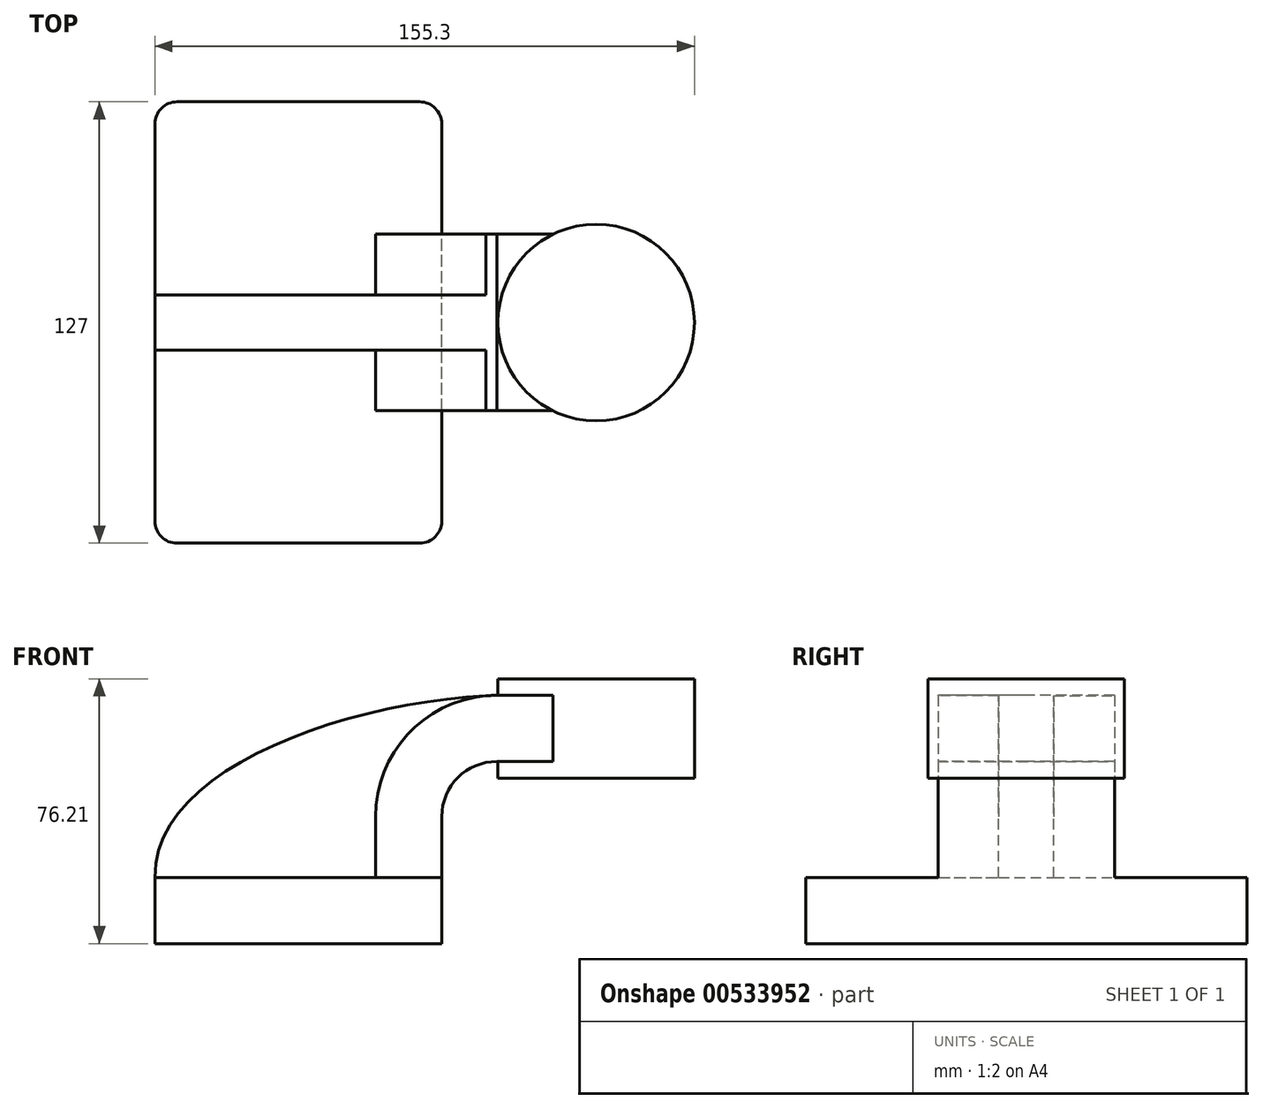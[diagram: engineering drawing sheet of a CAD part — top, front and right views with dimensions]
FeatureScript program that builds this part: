
annotation { "Feature Type Name" : "Feature", "Feature Type Description" : "" }
export const myFeature = defineFeature(function(context is Context, id is Id, definition is map)
    precondition{}
    {
        {
            var Q0;
            Q0=qCreatedBy(makeId("Front.planeOp"),FACE);
            var sketch = newSketch(context, id + "F0", { "sketchPlane" : qUnion([Q0])});
            skLineSegment(sketch, "E0.bottom", {"start": v(-41.28, 9.52) * mm, "end": v(41.27, 9.53) * mm});
            skLineSegment(sketch, "E0.top", {"start": v(-41.28, -9.52) * mm, "end": v(41.28, -9.52) * mm});
            skLineSegment(sketch, "E0.left", {"start": v(-41.28, 9.52) * mm, "end": v(-41.28, -9.53) * mm});
            skLineSegment(sketch, "E0.right", {"start": v(41.27, 9.53) * mm, "end": v(41.28, -9.52) * mm});
            skPoint(sketch, "E0.middle", {"position": v(0, 0) * mm});
            skLineSegment(sketch, "E1.bottom", {"start": v(63.22, 66.68) * mm, "end": v(114.02, 66.68) * mm});
            skLineSegment(sketch, "E1.top", {"start": v(63.22, 38.1) * mm, "end": v(114.02, 38.1) * mm});
            skLineSegment(sketch, "E1.left", {"start": v(63.22, 66.68) * mm, "end": v(63.22, 38.1) * mm});
            skLineSegment(sketch, "E1.right", {"start": v(114.02, 66.68) * mm, "end": v(114.02, 38.1) * mm});
            skPoint(sketch, "E1.middle", {"position": v(88.62, 52.39) * mm});
            skLineSegment(sketch, "E2", {"start": v(41.27, 9.53) * mm, "end": v(41.27, 27) * mm});
            skArc(sketch, "E3", {"start": v(41.27, 27) * mm, "mid": v(45.92, 38.23) * mm, "end": v(57.15, 42.88) * mm});
            skLineSegment(sketch, "E4", {"start": v(57.15, 42.88) * mm, "end": v(85.72, 42.88) * mm});
            skLineSegment(sketch, "E5.0", {"start": v(57.15, 61.93) * mm, "end": v(85.72, 61.93) * mm});
            skArc(sketch, "E5.1", {"start": v(22.22, 27) * mm, "mid": v(32.45, 51.7) * mm, "end": v(57.15, 61.93) * mm});
            skLineSegment(sketch, "E5.2", {"start": v(22.22, 9.53) * mm, "end": v(22.22, 27) * mm});
            skLineSegment(sketch, "E6", {"start": v(85.72, 38.1) * mm, "end": v(85.72, 61.93) * mm});
            skPoint(sketch, "E6.startSnap0", {"position": v(88.62, 38.1) * mm});
            skLineSegment(sketch, "E7", {"start": v(85.72, 61.93) * mm, "end": v(85.72, 66.68) * mm});
            skPoint(sketch, "E7.endSnap0", {"position": v(88.62, 66.68) * mm});
            skFitSpline(sketch, "E8", {"points": [v(-41.28, 9.52) * mm, v(57.15, 61.93) * mm], "startDerivative": vector(-1.63, 94.81) * mm, "endDerivative": vector(127.33, 4.49) * mm});
            skSolve(sketch);
        }
        {
            var Q0;
            Q0=makeQuery(id+"F0.imprint","IMPRINT",FACE,{"disambiguationData":[TD([[makeQuery(id+"F0.imprint","IMPRINT",EDGE,{"derivedFrom":sQuery(id+"F0.wireOp",EDGE,"E0.top")}),1.0]])]});
            extrude(context, id + "F1", {"entities" : qUnion([Q0]), "endBound" : BoundingType.SYMMETRIC, "depth" : 127 * mm, "offsetDistance" : 25.4 * mm});
        }
        {
            var Q0;
            {var subQ1=sQuery(id+"F0.wireOp",EDGE,"E2");Q0=makeQuery(id+"F0.imprint","IMPRINT",FACE,{"disambiguationData":[TD([[makeQuery(id+"F0.imprint","IMPRINT",EDGE,{"derivedFrom":subQ1}),1.0]])]});}
            var Q1;
            {var subQ0=sQuery(id+"F0.wireOp",EDGE,"E5.0");var subQ1=sQuery(id+"F0.wireOp",EDGE,"E1.left");var subQ2=makeQuery(id+"F0.imprint","INTERSECT",VERTEX,{"derivedFrom":[subQ1,subQ0]});Q1=makeQuery(id+"F0.imprint","IMPRINT",FACE,{"disambiguationData":[TD([[makeQuery(id+"F0.imprint","IMPRINT",EDGE,{"disambiguationData":[TD([[subQ2,-1.0]])],"derivedFrom":subQ1}),1.0]])]});}
            extrude(context, id + "F2", {"entities" : qUnion([Q0, Q1]), "operationType" : NewBodyOperationType.ADD, "endBound" : BoundingType.SYMMETRIC, "depth" : 50.8 * mm, "offsetDistance" : 25.4 * mm});
        }
        {
            var Q0;
            {var subQ3=sQuery(id+"F0.wireOp",EDGE,"E5.2");Q0=makeQuery(id+"F0.imprint","IMPRINT",FACE,{"disambiguationData":[TD([[makeQuery(id+"F0.imprint","IMPRINT",EDGE,{"derivedFrom":subQ3}),1.0]])]});}
            extrude(context, id + "F3", {"entities" : qUnion([Q0]), "operationType" : NewBodyOperationType.ADD, "endBound" : BoundingType.SYMMETRIC, "depth" : 15.88 * mm, "offsetDistance" : 25.4 * mm});
        }
        {
            var Q0;
            {var subQ4=sQuery(id+"F0.wireOp",EDGE,"E1.right");Q0=makeQuery(id+"F0.imprint","IMPRINT",FACE,{"disambiguationData":[TD([[makeQuery(id+"F0.imprint","IMPRINT",EDGE,{"derivedFrom":subQ4}),-1.0]])]});}
            var Q1;
            Q1=sQuery(id+"F0.wireOp",EDGE,"E6");
            revolve(context, id + "F4", {"operationType" : NewBodyOperationType.ADD, "entities" : qUnion([Q0]), "axis" : qUnion([Q1]), "revolveType" : RevolveType.FULL});
        }
        {
            var Q0;
            Q0=makeQuery(id+"F1.opExtrude","CAP_EDGE",EDGE,{"disambiguationData":[OSD([sQuery(id+"F0.wireOp",EDGE,"E0.right")])],"isStart":false});
            var Q1;
            Q1=makeQuery(id+"F1.opExtrude","CAP_EDGE",EDGE,{"disambiguationData":[OSD([sQuery(id+"F0.wireOp",EDGE,"E0.left")])],"isStart":false});
            var Q2;
            Q2=makeQuery(id+"F1.opExtrude","CAP_EDGE",EDGE,{"disambiguationData":[OSD([sQuery(id+"F0.wireOp",EDGE,"E0.right")])],"isStart":true});
            var Q3;
            Q3=makeQuery(id+"F1.opExtrude","CAP_EDGE",EDGE,{"disambiguationData":[OSD([sQuery(id+"F0.wireOp",EDGE,"E0.left")])],"isStart":true});
            fillet(context, id + "F5", {"entities" : qUnion([Q0, Q1, Q2, Q3]), "radius" : 6.35 * mm, "tangentPropagation" : true, "allowEdgeOverflow" : false});
        }
    });
